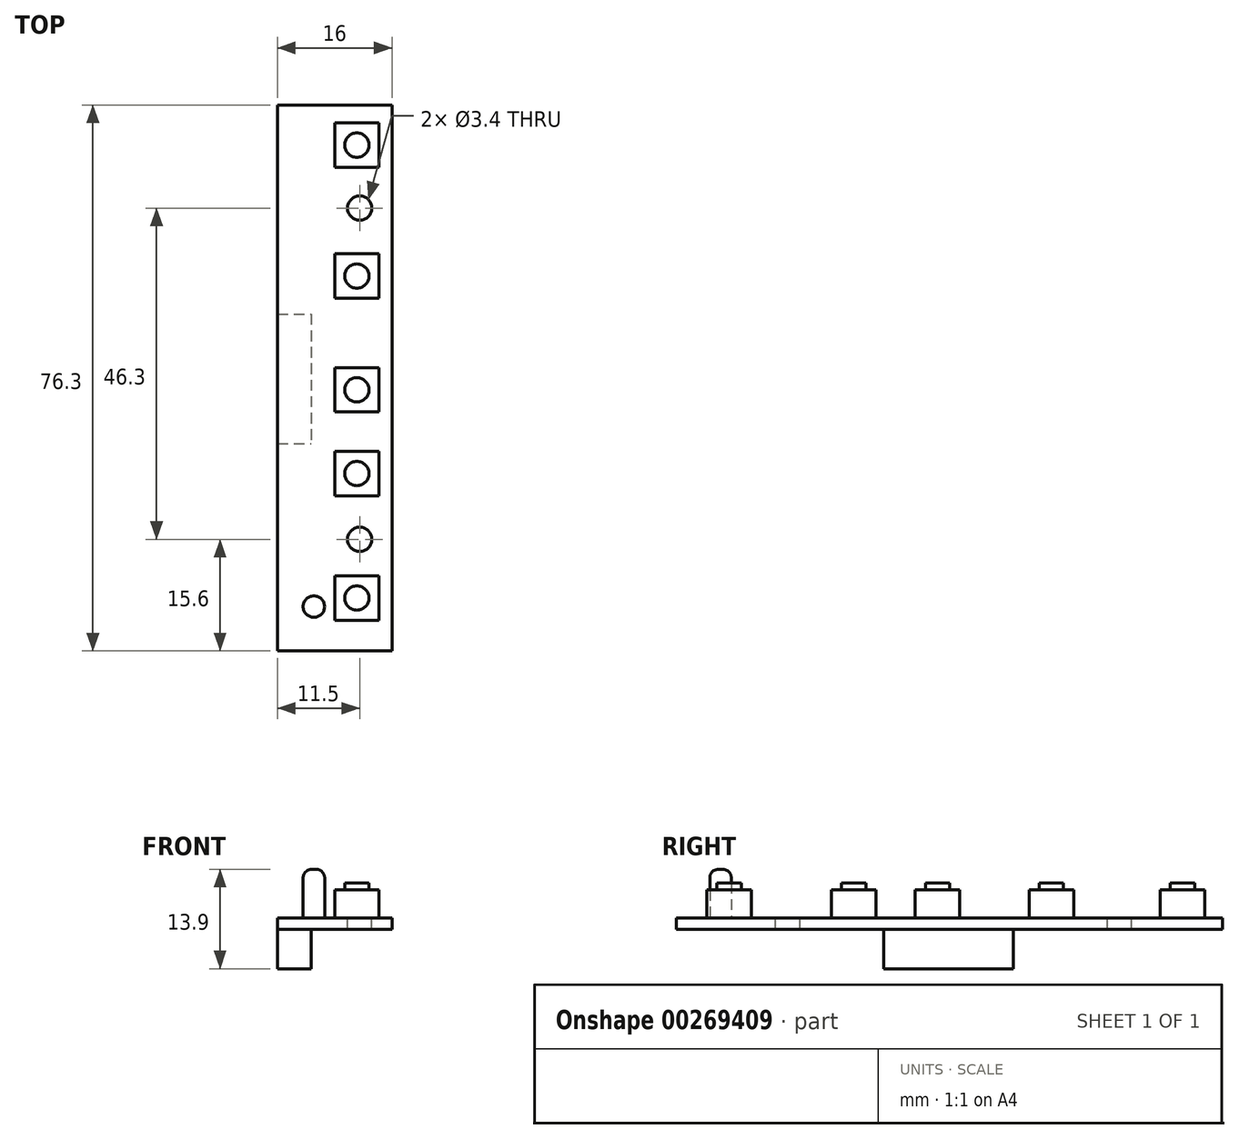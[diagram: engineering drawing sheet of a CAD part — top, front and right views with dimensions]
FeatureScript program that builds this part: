
annotation { "Feature Type Name" : "Feature", "Feature Type Description" : "" }
export const myFeature = defineFeature(function(context is Context, id is Id, definition is map)
    precondition{}
    {
        {
            var Q0;
            Q0=qCreatedBy(makeId("Top.planeOp"),FACE);
            var sketch = newSketch(context, id + "F0", { "sketchPlane" : qUnion([Q0])});
            skLineSegment(sketch, "E0.bottom", {"start": v(8, 38.15) * mm, "end": v(-8, 38.15) * mm});
            skLineSegment(sketch, "E0.top", {"start": v(8, -38.15) * mm, "end": v(-8, -38.15) * mm});
            skLineSegment(sketch, "E0.left", {"start": v(8, 38.15) * mm, "end": v(8, -38.15) * mm});
            skLineSegment(sketch, "E0.right", {"start": v(-8, 38.15) * mm, "end": v(-8, -38.15) * mm});
            skPoint(sketch, "E0.middle", {"position": v(0, 0) * mm});
            skCircle(sketch, "E1", {"center": v(3.5, 23.75) * mm, "radius": 1.7 * mm});
            skCircle(sketch, "E2", {"center": v(3.5, -22.55) * mm, "radius": 1.7 * mm});
            skSolve(sketch);
        }
        {
            var Q0;
            Q0=makeQuery(id+"F0.imprint","IMPRINT",FACE,{"disambiguationData":[TD([[makeQuery(id+"F0.imprint","IMPRINT",EDGE,{"derivedFrom":sQuery(id+"F0.wireOp",EDGE,"E0.bottom")}),1.0]])]});
            extrude(context, id + "F1", {"entities" : qUnion([Q0]), "oppositeDirection" : true, "depth" : 1.6 * mm});
        }
        {
            var Q0;
            Q0=makeQuery(id+"F1.opExtrude","CAP_FACE",FACE,{"disambiguationData":[OSD([sQuery(id+"F0.wireOp",EDGE,"E0.bottom"),sQuery(id+"F0.wireOp",EDGE,"E0.top"),sQuery(id+"F0.wireOp",EDGE,"E0.left"),sQuery(id+"F0.wireOp",EDGE,"E0.right")])],"isStart":true});
            var sketch = newSketch(context, id + "F2", { "sketchPlane" : qUnion([Q0])});
            skLineSegment(sketch, "E3.bottom", {"start": v(6.2, 29.45) * mm, "end": v(0, 29.45) * mm});
            skLineSegment(sketch, "E3.top", {"start": v(6.2, 35.65) * mm, "end": v(0, 35.65) * mm});
            skLineSegment(sketch, "E3.left", {"start": v(6.2, 29.45) * mm, "end": v(6.2, 35.65) * mm});
            skLineSegment(sketch, "E3.right", {"start": v(0, 29.45) * mm, "end": v(0, 35.65) * mm});
            skLineSegment(sketch, "E4.bottom", {"start": v(6.2, 17.35) * mm, "end": v(0, 17.35) * mm});
            skLineSegment(sketch, "E4.top", {"start": v(6.2, 11.15) * mm, "end": v(0, 11.15) * mm});
            skLineSegment(sketch, "E4.left", {"start": v(6.2, 17.35) * mm, "end": v(6.2, 11.15) * mm});
            skLineSegment(sketch, "E4.right", {"start": v(0, 17.35) * mm, "end": v(0, 11.15) * mm});
            skLineSegment(sketch, "E5.bottom", {"start": v(6.2, 1.45) * mm, "end": v(0, 1.45) * mm});
            skLineSegment(sketch, "E5.top", {"start": v(6.2, -4.75) * mm, "end": v(0, -4.75) * mm});
            skLineSegment(sketch, "E5.left", {"start": v(6.2, 1.45) * mm, "end": v(6.2, -4.75) * mm});
            skLineSegment(sketch, "E5.right", {"start": v(0, 1.45) * mm, "end": v(0, -4.75) * mm});
            skLineSegment(sketch, "E6.bottom", {"start": v(6.2, -10.25) * mm, "end": v(0, -10.25) * mm});
            skLineSegment(sketch, "E6.top", {"start": v(6.2, -16.45) * mm, "end": v(0, -16.45) * mm});
            skLineSegment(sketch, "E6.left", {"start": v(6.2, -10.25) * mm, "end": v(6.2, -16.45) * mm});
            skLineSegment(sketch, "E6.right", {"start": v(0, -10.25) * mm, "end": v(0, -16.45) * mm});
            skLineSegment(sketch, "E7.bottom", {"start": v(6.2, -27.65) * mm, "end": v(0, -27.65) * mm});
            skLineSegment(sketch, "E7.top", {"start": v(6.2, -33.85) * mm, "end": v(0, -33.85) * mm});
            skLineSegment(sketch, "E7.left", {"start": v(6.2, -27.65) * mm, "end": v(6.2, -33.85) * mm});
            skLineSegment(sketch, "E7.right", {"start": v(0, -27.65) * mm, "end": v(0, -33.85) * mm});
            skCircle(sketch, "E8", {"center": v(-2.9, -31.95) * mm, "radius": 1.5 * mm});
            skCircle(sketch, "E9", {"center": v(3.1, -30.75) * mm, "radius": 1.7 * mm});
            skCircle(sketch, "E10", {"center": v(3.1, -13.35) * mm, "radius": 1.7 * mm});
            skPoint(sketch, "E10.centerSnap0", {"position": v(3.1, -10.25) * mm});
            skPoint(sketch, "E10.centerSnap1", {"position": v(6.2, -13.35) * mm});
            skCircle(sketch, "E11", {"center": v(3.1, -1.65) * mm, "radius": 1.7 * mm});
            skPoint(sketch, "E11.centerSnap0", {"position": v(6.2, -1.65) * mm});
            skPoint(sketch, "E11.centerSnap1", {"position": v(3.1, 1.45) * mm});
            skCircle(sketch, "E12", {"center": v(3.1, 14.25) * mm, "radius": 1.7 * mm});
            skPoint(sketch, "E12.centerSnap0", {"position": v(3.1, 17.35) * mm});
            skPoint(sketch, "E12.centerSnap1", {"position": v(6.2, 14.25) * mm});
            skCircle(sketch, "E13", {"center": v(3.1, 32.55) * mm, "radius": 1.7 * mm});
            skPoint(sketch, "E13.centerSnap0", {"position": v(3.1, 29.45) * mm});
            skPoint(sketch, "E13.centerSnap1", {"position": v(6.2, 32.55) * mm});
            skSolve(sketch);
        }
        {
            var Q0;
            Q0=makeQuery(id+"F2.imprint","IMPRINT",FACE,{"disambiguationData":[TD([[makeQuery(id+"F2.imprint","IMPRINT",EDGE,{"derivedFrom":sQuery(id+"F2.wireOp",EDGE,"E7.bottom")}),1.0]])]});
            var Q1;
            Q1=makeQuery(id+"F2.imprint","IMPRINT",FACE,{"disambiguationData":[TD([[makeQuery(id+"F2.imprint","IMPRINT",EDGE,{"derivedFrom":sQuery(id+"F2.wireOp",EDGE,"E6.bottom")}),1.0]])]});
            var Q2;
            Q2=makeQuery(id+"F2.imprint","IMPRINT",FACE,{"disambiguationData":[TD([[makeQuery(id+"F2.imprint","IMPRINT",EDGE,{"derivedFrom":sQuery(id+"F2.wireOp",EDGE,"E5.bottom")}),1.0]])]});
            var Q3;
            Q3=makeQuery(id+"F2.imprint","IMPRINT",FACE,{"disambiguationData":[TD([[makeQuery(id+"F2.imprint","IMPRINT",EDGE,{"derivedFrom":sQuery(id+"F2.wireOp",EDGE,"E4.bottom")}),1.0]])]});
            var Q4;
            Q4=makeQuery(id+"F2.imprint","IMPRINT",FACE,{"disambiguationData":[TD([[makeQuery(id+"F2.imprint","IMPRINT",EDGE,{"derivedFrom":sQuery(id+"F2.wireOp",EDGE,"E3.bottom")}),-1.0]])]});
            extrude(context, id + "F3", {"entities" : qUnion([Q0, Q1, Q2, Q3, Q4]), "operationType" : NewBodyOperationType.ADD, "depth" : 3.9 * mm});
        }
        {
            var Q0;
            Q0=makeQuery(id+"F2.imprint","IMPRINT",FACE,{"disambiguationData":[TD([[makeQuery(id+"F2.imprint","IMPRINT",EDGE,{"derivedFrom":sQuery(id+"F2.wireOp",EDGE,"E13")}),1.0]])]});
            var Q1;
            Q1=makeQuery(id+"F2.imprint","IMPRINT",FACE,{"disambiguationData":[TD([[makeQuery(id+"F2.imprint","IMPRINT",EDGE,{"derivedFrom":sQuery(id+"F2.wireOp",EDGE,"E12")}),1.0]])]});
            var Q2;
            Q2=makeQuery(id+"F2.imprint","IMPRINT",FACE,{"disambiguationData":[TD([[makeQuery(id+"F2.imprint","IMPRINT",EDGE,{"derivedFrom":sQuery(id+"F2.wireOp",EDGE,"E11")}),1.0]])]});
            var Q3;
            Q3=makeQuery(id+"F2.imprint","IMPRINT",FACE,{"disambiguationData":[TD([[makeQuery(id+"F2.imprint","IMPRINT",EDGE,{"derivedFrom":sQuery(id+"F2.wireOp",EDGE,"E10")}),1.0]])]});
            var Q4;
            Q4=makeQuery(id+"F2.imprint","IMPRINT",FACE,{"disambiguationData":[TD([[makeQuery(id+"F2.imprint","IMPRINT",EDGE,{"derivedFrom":sQuery(id+"F2.wireOp",EDGE,"E9")}),1.0]])]});
            extrude(context, id + "F4", {"entities" : qUnion([Q0, Q1, Q2, Q3, Q4]), "operationType" : NewBodyOperationType.ADD, "depth" : 4.9 * mm});
        }
        {
            var Q0;
            Q0=makeQuery(id+"F2.imprint","IMPRINT",FACE,{"disambiguationData":[TD([[makeQuery(id+"F2.imprint","IMPRINT",EDGE,{"derivedFrom":sQuery(id+"F2.wireOp",EDGE,"E8")}),1.0]])]});
            extrude(context, id + "F5", {"entities" : qUnion([Q0]), "operationType" : NewBodyOperationType.ADD, "depth" : 6.8 * mm});
        }
        {
            var Q0;
            Q0=makeQuery(id+"F5.opExtrude","CAP_EDGE",EDGE,{"disambiguationData":[OSD([sQuery(id+"F2.wireOp",EDGE,"E8")])],"isStart":false});
            fillet(context, id + "F6", {"entities" : qUnion([Q0]), "radius" : 1.2 * mm, "tangentPropagation" : true, "allowEdgeOverflow" : false});
        }
        {
            var Q0;
            Q0=makeQuery(id+"F1.opExtrude","CAP_FACE",FACE,{"disambiguationData":[OSD([sQuery(id+"F0.wireOp",EDGE,"E0.bottom"),sQuery(id+"F0.wireOp",EDGE,"E0.top"),sQuery(id+"F0.wireOp",EDGE,"E0.left"),sQuery(id+"F0.wireOp",EDGE,"E0.right"),sQuery(id+"F0.wireOp",EDGE,"E1"),sQuery(id+"F0.wireOp",EDGE,"E2")])],"isStart":false});
            var sketch = newSketch(context, id + "F7", { "sketchPlane" : qUnion([Q0])});
            skLineSegment(sketch, "E14.bottom", {"start": v(-8, -8.95) * mm, "end": v(-3.3, -8.95) * mm});
            skLineSegment(sketch, "E14.top", {"start": v(-8, 9.15) * mm, "end": v(-3.3, 9.15) * mm});
            skLineSegment(sketch, "E14.left", {"start": v(-8, -8.95) * mm, "end": v(-8, 9.15) * mm});
            skLineSegment(sketch, "E14.right", {"start": v(-3.3, -8.95) * mm, "end": v(-3.3, 9.15) * mm});
            skSolve(sketch);
        }
        {
            var Q0;
            Q0=makeQuery(id+"F7.imprint","IMPRINT",FACE,{"disambiguationData":[TD([[makeQuery(id+"F7.imprint","IMPRINT",EDGE,{"derivedFrom":sQuery(id+"F7.wireOp",EDGE,"E14.bottom")}),1.0]])]});
            extrude(context, id + "F8", {"entities" : qUnion([Q0]), "operationType" : NewBodyOperationType.ADD, "depth" : 5.5 * mm});
        }
    });
